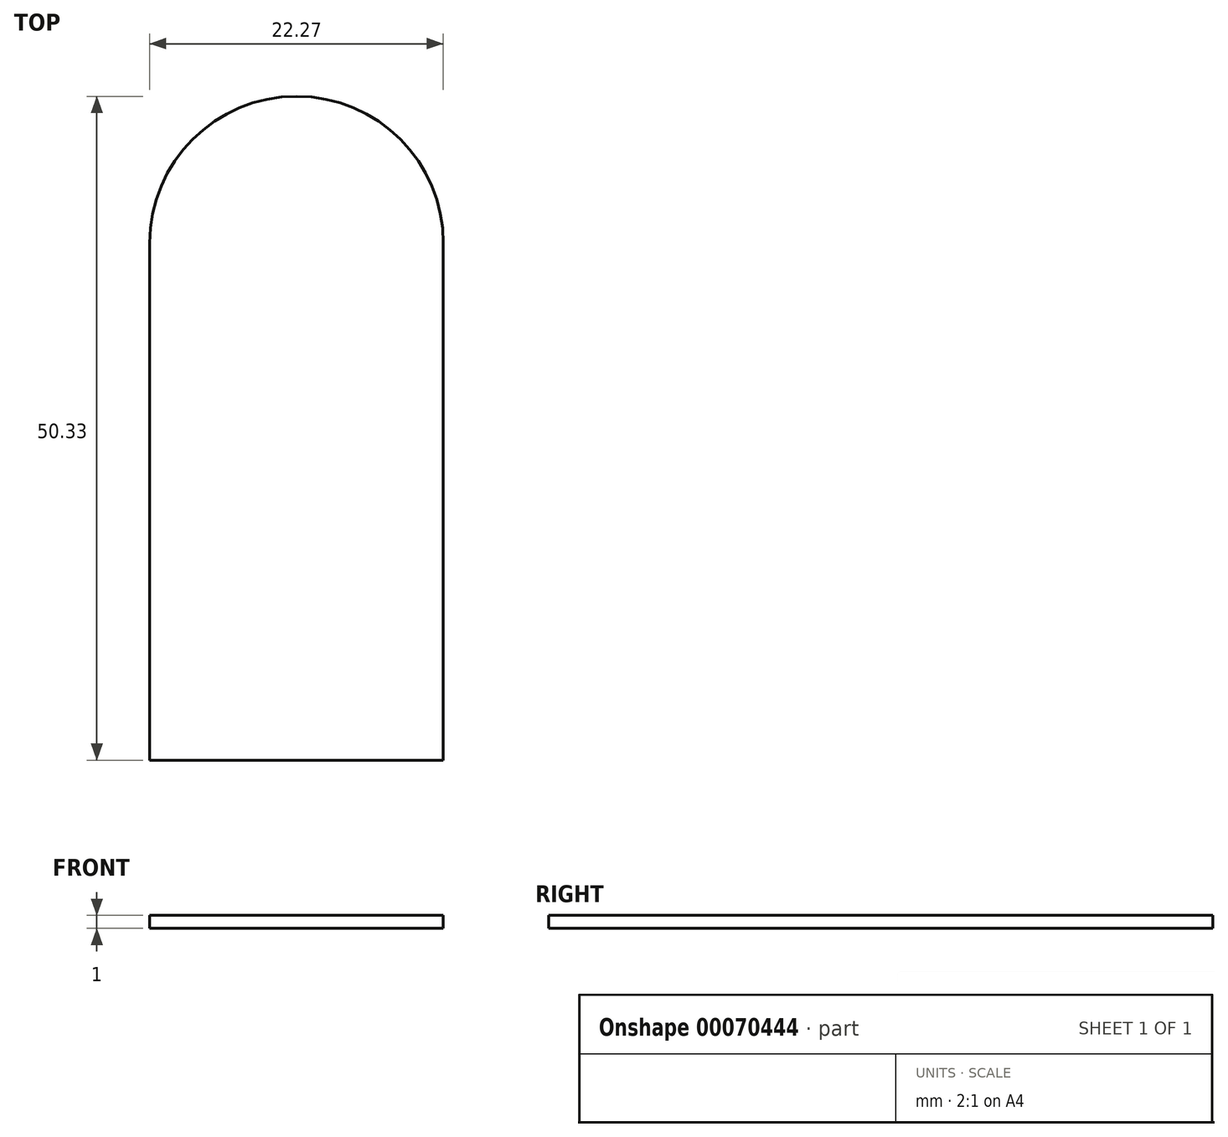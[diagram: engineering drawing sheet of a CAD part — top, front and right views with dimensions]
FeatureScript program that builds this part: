
annotation { "Feature Type Name" : "Feature", "Feature Type Description" : "" }
export const myFeature = defineFeature(function(context is Context, id is Id, definition is map)
    precondition{}
    {
        {
            var Q0;
            Q0=qCreatedBy(makeId("Top.planeOp"),FACE);
            var sketch = newSketch(context, id + "F0", { "sketchPlane" : qUnion([Q0])});
            skCircle(sketch, "E0", {"center": v(-44.85, -19.9) * mm, "radius": 11.13 * mm});
            skLineSegment(sketch, "E1.bottom", {"start": v(-55.99, -19.9) * mm, "end": v(-33.72, -19.9) * mm});
            skLineSegment(sketch, "E1.top", {"start": v(-55.99, -59.09) * mm, "end": v(-33.72, -59.09) * mm});
            skLineSegment(sketch, "E1.left", {"start": v(-55.99, -19.9) * mm, "end": v(-55.99, -59.09) * mm});
            skLineSegment(sketch, "E1.right", {"start": v(-33.72, -19.9) * mm, "end": v(-33.72, -59.09) * mm});
            skSolve(sketch);
        }
        {
            var Q0;
            Q0 = qSketchRegion(id + "F0", true);
            extrude(context, id + "F1", {"entities" : qUnion([Q0]), "depth" : 1 * mm});
        }
    });
